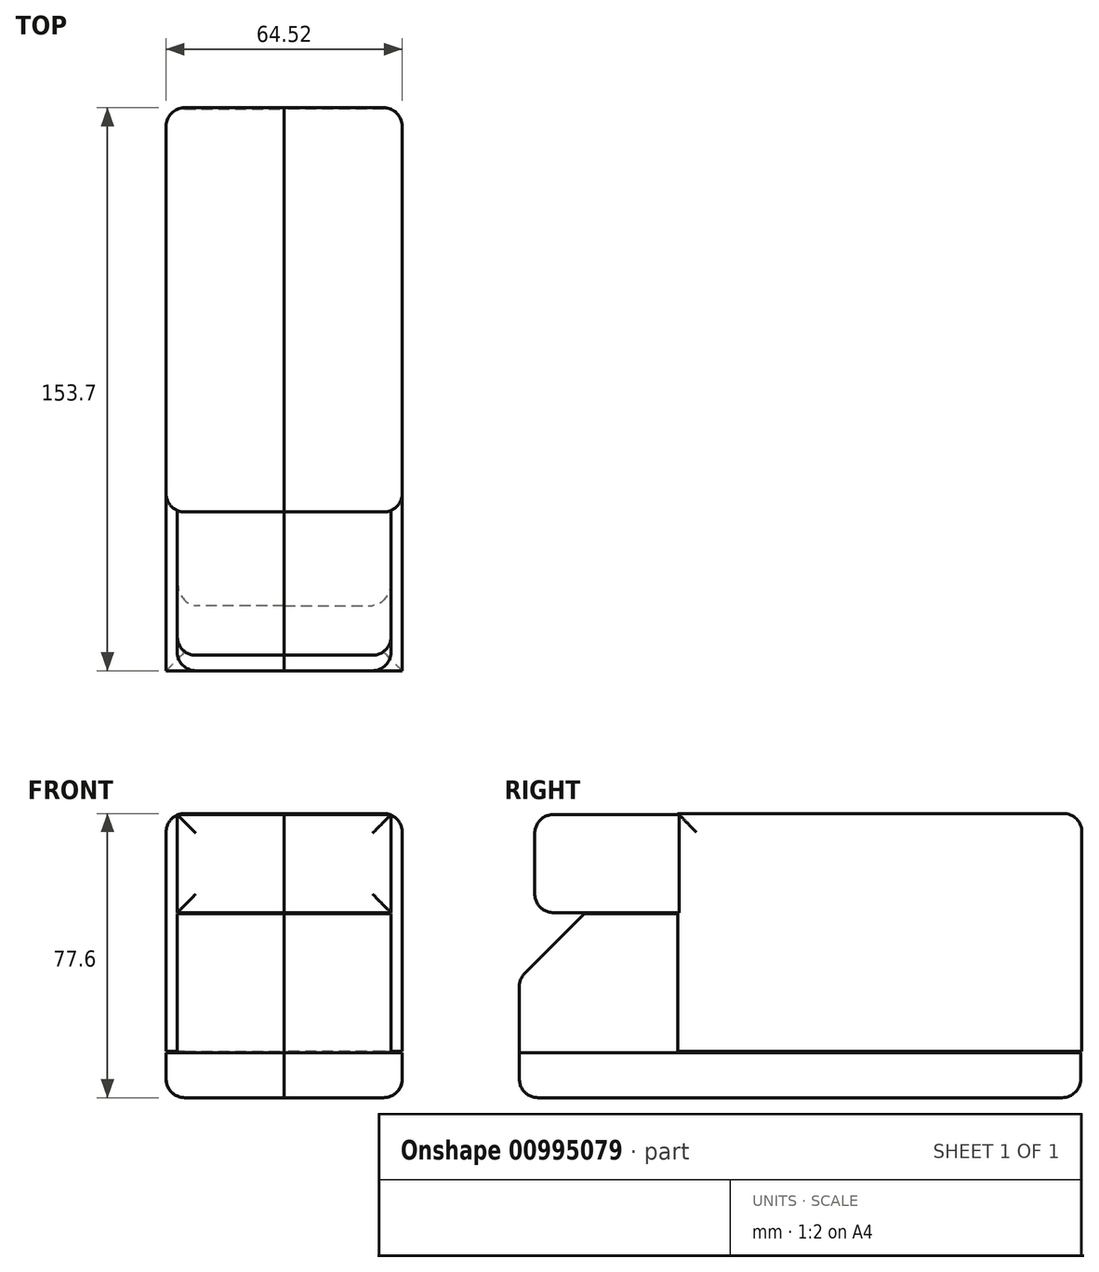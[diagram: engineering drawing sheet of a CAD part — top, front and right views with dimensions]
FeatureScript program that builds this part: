
annotation { "Feature Type Name" : "Feature", "Feature Type Description" : "" }
export const myFeature = defineFeature(function(context is Context, id is Id, definition is map)
    precondition{}
    {
        {
            var Q0;
            Q0=qCreatedBy(makeId("Right.planeOp"),FACE);
            var sketch = newSketch(context, id + "F0", { "sketchPlane" : qUnion([Q0])});
            skLineSegment(sketch, "E0.bottom", {"start": v(-34.44, 49.18) * mm, "end": v(75.95, 49.18) * mm});
            skLineSegment(sketch, "E0.top", {"start": v(-34.44, -15.8) * mm, "end": v(75.95, -15.8) * mm});
            skLineSegment(sketch, "E0.left", {"start": v(-34.44, 49.18) * mm, "end": v(-34.44, -15.8) * mm});
            skLineSegment(sketch, "E0.right", {"start": v(75.95, 49.18) * mm, "end": v(75.95, -15.8) * mm});
            skSolve(sketch);
        }
        {
            var Q0;
            Q0=qCreatedBy(makeId("Right.planeOp"),FACE);
            var sketch = newSketch(context, id + "F1", { "sketchPlane" : qUnion([Q0])});
            skCircle(sketch, "E1", {"center": v(-48.88, -26.92) * mm, "radius": 6.38 * mm});
            skCircle(sketch, "E2", {"center": v(-48.88, -26.92) * mm, "radius": 10.87 * mm});
            skCircle(sketch, "E3", {"center": v(30.53, -29.33) * mm, "radius": 5.79 * mm});
            skCircle(sketch, "E4", {"center": v(30.53, -29.33) * mm, "radius": 11.57 * mm});
            skSolve(sketch);
        }
        {
            var Q0;
            Q0=qCreatedBy(makeId("Right.planeOp"),FACE);
            var sketch = newSketch(context, id + "F2", { "sketchPlane" : qUnion([Q0])});
            skLineSegment(sketch, "E5.bottom", {"start": v(-34.44, -16.1) * mm, "end": v(-77.75, -16.1) * mm});
            skLineSegment(sketch, "E5.top", {"start": v(-34.44, 21.8) * mm, "end": v(-77.75, 21.8) * mm});
            skLineSegment(sketch, "E5.left", {"start": v(-34.44, -16.1) * mm, "end": v(-34.44, 21.8) * mm});
            skLineSegment(sketch, "E5.right", {"start": v(-77.75, -16.1) * mm, "end": v(-77.75, 21.8) * mm});
            skSolve(sketch);
        }
        {
            var Q0;
            Q0=qCreatedBy(makeId("Right.planeOp"),FACE);
            var sketch = newSketch(context, id + "F3", { "sketchPlane" : qUnion([Q0])});
            skLineSegment(sketch, "E6.bottom", {"start": v(-34.44, 22.1) * mm, "end": v(-73.54, 22.1) * mm});
            skLineSegment(sketch, "E6.top", {"start": v(-34.44, 48.88) * mm, "end": v(-73.54, 48.88) * mm});
            skLineSegment(sketch, "E6.left", {"start": v(-34.44, 22.1) * mm, "end": v(-34.44, 48.88) * mm});
            skLineSegment(sketch, "E6.right", {"start": v(-73.54, 22.1) * mm, "end": v(-73.54, 48.88) * mm});
            skSolve(sketch);
        }
        {
            var Q0;
            Q0=qCreatedBy(makeId("Right.planeOp"),FACE);
            var sketch = newSketch(context, id + "F4", { "sketchPlane" : qUnion([Q0])});
            skLineSegment(sketch, "E7.bottom", {"start": v(-77.75, -16.1) * mm, "end": v(75.65, -16.1) * mm});
            skLineSegment(sketch, "E7.top", {"start": v(-77.75, -28.42) * mm, "end": v(75.65, -28.42) * mm});
            skLineSegment(sketch, "E7.left", {"start": v(-77.75, -16.1) * mm, "end": v(-77.75, -28.42) * mm});
            skLineSegment(sketch, "E7.right", {"start": v(75.65, -16.1) * mm, "end": v(75.65, -28.42) * mm});
            skSolve(sketch);
        }
        {
            var Q0;
            Q0=makeQuery(id+"F0.imprint","IMPRINT",FACE,{"disambiguationData":[TD([[makeQuery(id+"F0.imprint","IMPRINT",EDGE,{"derivedFrom":sQuery(id+"F0.wireOp",EDGE,"E0.bottom")}),-1.0]])]});
            extrude(context, id + "F5", {"entities" : qUnion([Q0]), "depth" : 32.26 * mm, "offsetDistance" : 25.4 * mm});
        }
        {
            var Q0;
            Q0=sQuery(id+"F1.wireOp",EDGE,"E1");
            var Q1;
            Q1=sQuery(id+"F1.wireOp",EDGE,"E2");
            extrude(context, id + "F6", {"bodyType" : ToolBodyType.SURFACE, "surfaceEntities" : qUnion([Q0, Q1]), "depth" : 8.9 * mm, "offsetDistance" : 25.4 * mm});
        }
        {
            var Q0;
            Q0=sQuery(id+"F1.wireOp",EDGE,"E4");
            var Q1;
            Q1=sQuery(id+"F1.wireOp",EDGE,"E3");
            extrude(context, id + "F7", {"bodyType" : ToolBodyType.SURFACE, "surfaceEntities" : qUnion([Q0, Q1]), "depth" : 8.9 * mm, "offsetDistance" : 25.4 * mm});
        }
        {
            var Q0;
            Q0=makeQuery(id+"F4.imprint","IMPRINT",FACE,{"disambiguationData":[TD([[makeQuery(id+"F4.imprint","IMPRINT",EDGE,{"derivedFrom":sQuery(id+"F4.wireOp",EDGE,"E7.bottom")}),-1.0]])]});
            extrude(context, id + "F8", {"entities" : qUnion([Q0]), "depth" : 32.26 * mm, "offsetDistance" : 25.4 * mm});
        }
        {
            var Q0;
            Q0=makeQuery(id+"F2.imprint","IMPRINT",FACE,{"disambiguationData":[TD([[makeQuery(id+"F2.imprint","IMPRINT",EDGE,{"derivedFrom":sQuery(id+"F2.wireOp",EDGE,"E5.bottom")}),-1.0]])]});
            extrude(context, id + "F9", {"entities" : qUnion([Q0]), "depth" : 29.2 * mm, "offsetDistance" : 25.4 * mm});
        }
        {
            var Q0;
            Q0=makeQuery(id+"F3.imprint","IMPRINT",FACE,{"disambiguationData":[TD([[makeQuery(id+"F3.imprint","IMPRINT",EDGE,{"derivedFrom":sQuery(id+"F3.wireOp",EDGE,"E6.bottom")}),-1.0]])]});
            extrude(context, id + "F10", {"entities" : qUnion([Q0]), "operationType" : NewBodyOperationType.ADD, "depth" : 29.2 * mm, "offsetDistance" : 25.4 * mm});
        }
        {
            var Q0;
            Q0=makeQuery(id+"F9.opExtrude","SWEPT_EDGE",EDGE,{"disambiguationData":[OSD([sQuery(id+"F2.wireOp",EDGE,"E5.top"),sQuery(id+"F2.wireOp",EDGE,"E5.right")])]});
            chamfer(context, id + "F11", {"entities" : qUnion([Q0]), "width" : 17.78 * mm, "tangentPropagation" : true});
        }
        {
            var Q0;
            Q0=makeQuery(id+"F10.opExtrude","SWEPT_EDGE",EDGE,{"disambiguationData":[OSD([sQuery(id+"F3.wireOp",EDGE,"E6.top"),sQuery(id+"F3.wireOp",EDGE,"E6.right")])]});
            var Q1;
            Q1=makeQuery(id+"F10.opExtrude","SWEPT_EDGE",EDGE,{"disambiguationData":[OSD([sQuery(id+"F3.wireOp",EDGE,"E6.bottom"),sQuery(id+"F3.wireOp",EDGE,"E6.right")])]});
            var Q2;
            Q2=makeQuery(id+"F8.opExtrude","CAP_EDGE",EDGE,{"disambiguationData":[OSD([sQuery(id+"F4.wireOp",EDGE,"E7.top")])],"isStart":false});
            var Q3;
            {var subQ0=sQuery(id+"F2.wireOp",EDGE,"E5.right");var subQ1=sQuery(id+"F2.wireOp",EDGE,"E5.top");Q3=makeQuery(id+"F11.opChamfer","BLEND_EDGE",EDGE,{"blendedFrom":[makeQuery(id+"F9.opExtrude","SWEPT_EDGE",EDGE,{"disambiguationData":[OSD([subQ1,subQ0])]}),makeQuery(id+"F9.opExtrude","CAP_FACE",FACE,{"disambiguationData":[OSD([sQuery(id+"F2.wireOp",EDGE,"E5.bottom"),subQ1,sQuery(id+"F2.wireOp",EDGE,"E5.left"),subQ0])],"isStart":false})],"blendedInto":[makeQuery(id+"F9.opExtrude","CAP_FACE",FACE,{"disambiguationData":[OSD([sQuery(id+"F2.wireOp",EDGE,"E5.bottom"),subQ1,sQuery(id+"F2.wireOp",EDGE,"E5.left"),subQ0])],"isStart":false})]});}
            var Q4;
            Q4=makeQuery(id+"F9.opExtrude","CAP_EDGE",EDGE,{"disambiguationData":[OSD([sQuery(id+"F2.wireOp",EDGE,"E5.right")])],"isStart":false});
            var Q5;
            {var subQ0=sQuery(id+"F2.wireOp",EDGE,"E5.right");Q5=makeQuery(id+"F11.opChamfer","BLEND_EDGE",EDGE,{"blendedFrom":[makeQuery(id+"F9.opExtrude","SWEPT_EDGE",EDGE,{"disambiguationData":[OSD([sQuery(id+"F2.wireOp",EDGE,"E5.top"),subQ0])]}),makeQuery(id+"F9.opExtrude","SWEPT_FACE",FACE,{"disambiguationData":[OSD([subQ0])]})],"blendedInto":[makeQuery(id+"F9.opExtrude","SWEPT_FACE",FACE,{"disambiguationData":[OSD([subQ0])]})]});}
            var Q6;
            Q6=makeQuery(id+"F8.opExtrude","SWEPT_EDGE",EDGE,{"disambiguationData":[OSD([sQuery(id+"F4.wireOp",EDGE,"E7.top"),sQuery(id+"F4.wireOp",EDGE,"E7.left")])]});
            var Q7;
            Q7=makeQuery(id+"F5.opExtrude","CAP_EDGE",EDGE,{"disambiguationData":[OSD([sQuery(id+"F0.wireOp",EDGE,"E0.left")])],"isStart":false});
            var Q8;
            Q8=makeQuery(id+"F5.opExtrude","CAP_EDGE",EDGE,{"disambiguationData":[OSD([sQuery(id+"F0.wireOp",EDGE,"E0.right")])],"isStart":false});
            var Q9;
            Q9=makeQuery(id+"F8.opExtrude","CAP_EDGE",EDGE,{"disambiguationData":[OSD([sQuery(id+"F4.wireOp",EDGE,"E7.right")])],"isStart":false});
            var Q10;
            Q10=makeQuery(id+"F10.opExtrude","CAP_EDGE",EDGE,{"disambiguationData":[OSD([sQuery(id+"F3.wireOp",EDGE,"E6.right")])],"isStart":false});
            var Q11;
            Q11=makeQuery(id+"F5.opExtrude","CAP_EDGE",EDGE,{"disambiguationData":[OSD([sQuery(id+"F0.wireOp",EDGE,"E0.bottom")])],"isStart":false});
            fillet(context, id + "F12", {"entities" : qUnion([Q0, Q1, Q2, Q3, Q4, Q5, Q6, Q7, Q8, Q9, Q10, Q11]), "radius" : 5.08 * mm, "tangentPropagation" : true, "allowEdgeOverflow" : false});
        }
        {
            var Q0;
            Q0=makeQuery(id+"F5.opExtrude","SWEPT_EDGE",EDGE,{"disambiguationData":[OSD([sQuery(id+"F0.wireOp",EDGE,"E0.bottom"),sQuery(id+"F0.wireOp",EDGE,"E0.right")])]});
            var Q1;
            Q1=makeQuery(id+"F8.opExtrude","SWEPT_EDGE",EDGE,{"disambiguationData":[OSD([sQuery(id+"F4.wireOp",EDGE,"E7.top"),sQuery(id+"F4.wireOp",EDGE,"E7.right")])]});
            fillet(context, id + "F13", {"entities" : qUnion([Q0, Q1]), "radius" : 5.08 * mm, "tangentPropagation" : true, "allowEdgeOverflow" : false});
        }
        {
            var Q0;
            Q0=makeQuery(id+"F5.opExtrude","SWEPT_BODY",BODY,{"disambiguationData":[OSD([sQuery(id+"F0.wireOp",EDGE,"E0.bottom"),sQuery(id+"F0.wireOp",EDGE,"E0.top"),sQuery(id+"F0.wireOp",EDGE,"E0.left"),sQuery(id+"F0.wireOp",EDGE,"E0.right")])]});
            var Q1;
            Q1=makeQuery(id+"F6.opExtrude","SWEPT_BODY",BODY,{"disambiguationData":[OSD([sQuery(id+"F1.wireOp",EDGE,"E1")])]});
            var Q2;
            Q2=makeQuery(id+"F6.opExtrude","SWEPT_BODY",BODY,{"disambiguationData":[OSD([sQuery(id+"F1.wireOp",EDGE,"E2")])]});
            var Q3;
            Q3=makeQuery(id+"F7.opExtrude","SWEPT_BODY",BODY,{"disambiguationData":[OSD([sQuery(id+"F1.wireOp",EDGE,"E3")])]});
            var Q4;
            Q4=makeQuery(id+"F7.opExtrude","SWEPT_BODY",BODY,{"disambiguationData":[OSD([sQuery(id+"F1.wireOp",EDGE,"E4")])]});
            var Q5;
            Q5=makeQuery(id+"F8.opExtrude","SWEPT_BODY",BODY,{"disambiguationData":[OSD([sQuery(id+"F4.wireOp",EDGE,"E7.bottom"),sQuery(id+"F4.wireOp",EDGE,"E7.top"),sQuery(id+"F4.wireOp",EDGE,"E7.left"),sQuery(id+"F4.wireOp",EDGE,"E7.right")])]});
            var Q6;
            Q6=makeQuery(id+"F9.opExtrude","SWEPT_BODY",BODY,{"disambiguationData":[OSD([sQuery(id+"F2.wireOp",EDGE,"E5.bottom"),sQuery(id+"F2.wireOp",EDGE,"E5.top"),sQuery(id+"F2.wireOp",EDGE,"E5.left"),sQuery(id+"F2.wireOp",EDGE,"E5.right")])]});
            var Q7;
            Q7=qCreatedBy(makeId("Right.planeOp"),FACE);
            mirror(context, id + "F14", {"entities" : qUnion([Q0, Q1, Q2, Q3, Q4, Q5, Q6]), "mirrorPlane" : qUnion([Q7])});
        }
    });
